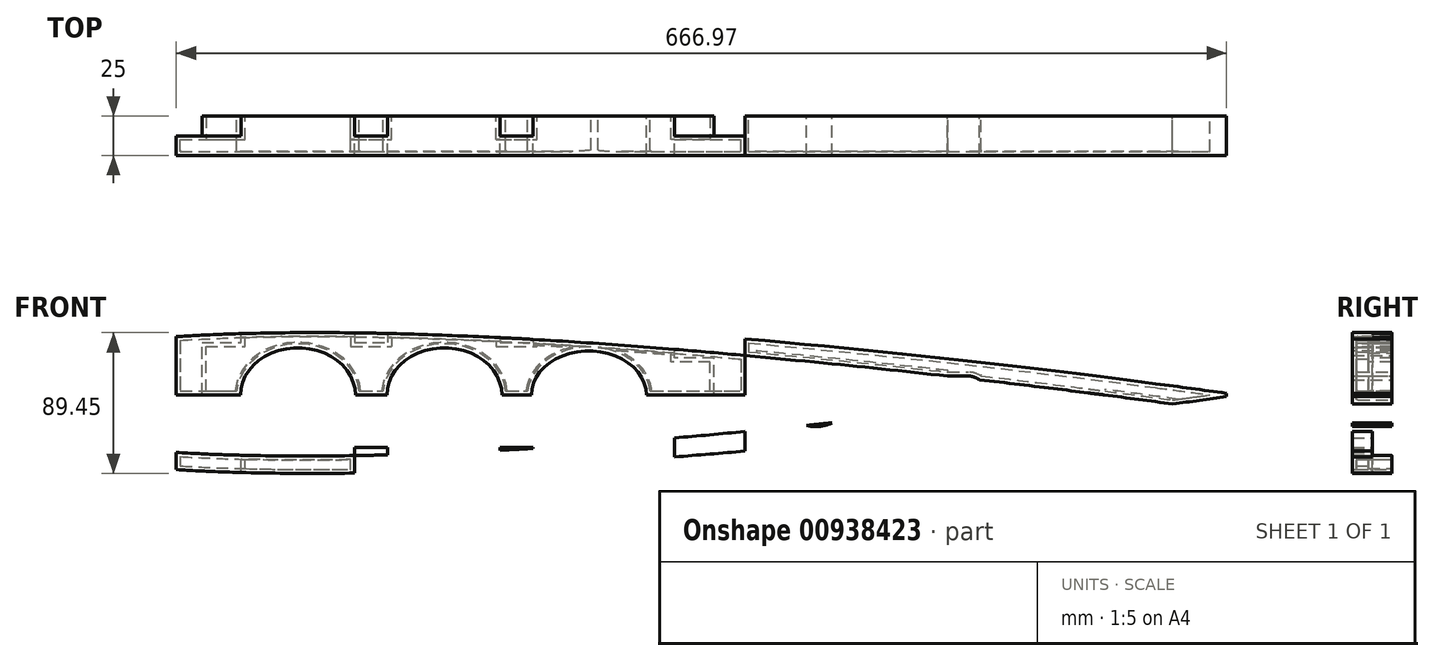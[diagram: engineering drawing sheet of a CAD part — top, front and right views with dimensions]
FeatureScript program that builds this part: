
annotation { "Feature Type Name" : "Feature", "Feature Type Description" : "" }
export const myFeature = defineFeature(function(context is Context, id is Id, definition is map)
    precondition{}
    {
        {
            var Q0;
            Q0=qCreatedBy(makeId("Front.planeOp"),FACE);
            var sketch = newSketch(context, id + "F0", { "sketchPlane" : qUnion([Q0])});
            skLineSegment(sketch, "E0", {"start": v(0, 0) * mm, "end": v(830, 0) * mm});
            skLineSegment(sketch, "E1", {"start": v(23.53, 0) * mm, "end": v(23.53, 22.98) * mm, "construction": true});
            skLineSegment(sketch, "E2", {"start": v(30.64, 0) * mm, "end": v(30.64, 25.86) * mm, "construction": true});
            skLineSegment(sketch, "E3", {"start": v(38.65, 0) * mm, "end": v(38.65, 28.62) * mm, "construction": true});
            skLineSegment(sketch, "E4", {"start": v(47.54, 0) * mm, "end": v(47.54, 31.24) * mm, "construction": true});
            skLineSegment(sketch, "E5", {"start": v(57.28, 0) * mm, "end": v(57.28, 33.72) * mm, "construction": true});
            skLineSegment(sketch, "E6", {"start": v(67.86, 0) * mm, "end": v(67.86, 36.05) * mm, "construction": true});
            skLineSegment(sketch, "E7", {"start": v(79.26, 0) * mm, "end": v(79.26, 38.22) * mm, "construction": true});
            skLineSegment(sketch, "E8", {"start": v(91.44, 0) * mm, "end": v(91.44, 40.22) * mm, "construction": true});
            skLineSegment(sketch, "E9", {"start": v(104.37, 0) * mm, "end": v(104.37, 42.04) * mm, "construction": true});
            skLineSegment(sketch, "E10", {"start": v(118.03, 0) * mm, "end": v(118.03, 43.68) * mm, "construction": true});
            skLineSegment(sketch, "E11", {"start": v(132.38, 0) * mm, "end": v(132.38, 45.13) * mm, "construction": true});
            skLineSegment(sketch, "E12", {"start": v(147.4, 0) * mm, "end": v(147.4, 46.38) * mm, "construction": true});
            skLineSegment(sketch, "E13", {"start": v(163.03, 0) * mm, "end": v(163.03, 47.45) * mm, "construction": true});
            skLineSegment(sketch, "E14", {"start": v(179.25, 0) * mm, "end": v(179.25, 48.31) * mm, "construction": true});
            skLineSegment(sketch, "E15", {"start": v(196.03, 0) * mm, "end": v(196.03, 48.98) * mm, "construction": true});
            skLineSegment(sketch, "E16", {"start": v(213.32, 0) * mm, "end": v(213.32, 49.45) * mm, "construction": true});
            skLineSegment(sketch, "E17", {"start": v(231.08, 0) * mm, "end": v(231.08, 49.73) * mm, "construction": true});
            skLineSegment(sketch, "E18", {"start": v(249.26, 0) * mm, "end": v(249.26, 49.81) * mm, "construction": true});
            skLineSegment(sketch, "E19", {"start": v(267.84, 0) * mm, "end": v(267.84, 49.72) * mm, "construction": true});
            skLineSegment(sketch, "E20", {"start": v(0.48, 0) * mm, "end": v(0.48, 3.54) * mm, "construction": true});
            skLineSegment(sketch, "E21", {"start": v(1.94, 0) * mm, "end": v(1.94, 7) * mm, "construction": true});
            skLineSegment(sketch, "E22", {"start": v(4.35, 0) * mm, "end": v(4.35, 10.38) * mm, "construction": true});
            skLineSegment(sketch, "E23", {"start": v(7.73, 0) * mm, "end": v(7.73, 13.67) * mm, "construction": true});
            skLineSegment(sketch, "E24", {"start": v(12.06, 0) * mm, "end": v(12.06, 16.87) * mm, "construction": true});
            skLineSegment(sketch, "E25", {"start": v(17.33, 0) * mm, "end": v(17.33, 19.98) * mm, "construction": true});
            skLineSegment(sketch, "E26", {"start": v(286.76, 0) * mm, "end": v(286.76, 49.45) * mm, "construction": true});
            skLineSegment(sketch, "E27", {"start": v(305.98, 0) * mm, "end": v(305.98, 49) * mm, "construction": true});
            skLineSegment(sketch, "E28", {"start": v(325.45, 0) * mm, "end": v(325.45, 48.4) * mm, "construction": true});
            skLineSegment(sketch, "E29", {"start": v(345.13, 0) * mm, "end": v(345.13, 47.64) * mm, "construction": true});
            skLineSegment(sketch, "E30", {"start": v(364.98, 0) * mm, "end": v(364.98, 46.75) * mm, "construction": true});
            skLineSegment(sketch, "E31", {"start": v(384.94, 0) * mm, "end": v(384.94, 45.71) * mm, "construction": true});
            skLineSegment(sketch, "E32", {"start": v(404.97, 0) * mm, "end": v(404.97, 44.56) * mm, "construction": true});
            skLineSegment(sketch, "E33", {"start": v(425.03, 0) * mm, "end": v(425.03, 43.3) * mm, "construction": true});
            skLineSegment(sketch, "E34", {"start": v(445.06, 0) * mm, "end": v(445.06, 41.93) * mm, "construction": true});
            skLineSegment(sketch, "E35", {"start": v(465.02, 0) * mm, "end": v(465.02, 40.47) * mm, "construction": true});
            skLineSegment(sketch, "E36", {"start": v(484.87, 0) * mm, "end": v(484.87, 38.94) * mm, "construction": true});
            skLineSegment(sketch, "E37", {"start": v(504.55, 0) * mm, "end": v(504.55, 37.33) * mm, "construction": true});
            skLineSegment(sketch, "E38", {"start": v(524.02, 0) * mm, "end": v(524.02, 35.67) * mm, "construction": true});
            skLineSegment(sketch, "E39", {"start": v(543.24, 0) * mm, "end": v(543.24, 33.96) * mm, "construction": true});
            skLineSegment(sketch, "E40", {"start": v(562.16, 0) * mm, "end": v(562.16, 32.21) * mm, "construction": true});
            skLineSegment(sketch, "E41", {"start": v(580.74, 0) * mm, "end": v(580.74, 30.44) * mm, "construction": true});
            skLineSegment(sketch, "E42", {"start": v(598.92, 0) * mm, "end": v(598.92, 28.64) * mm, "construction": true});
            skLineSegment(sketch, "E43", {"start": v(633.97, 0) * mm, "end": v(633.97, 25.03) * mm, "construction": true});
            skLineSegment(sketch, "E44", {"start": v(616.68, 0) * mm, "end": v(616.68, 26.83) * mm, "construction": true});
            skLineSegment(sketch, "E45", {"start": v(650.75, 0) * mm, "end": v(650.75, 23.23) * mm, "construction": true});
            skLineSegment(sketch, "E46", {"start": v(666.97, 0) * mm, "end": v(666.97, 21.44) * mm, "construction": true});
            skLineSegment(sketch, "E47", {"start": v(682.6, 0) * mm, "end": v(682.6, 19.68) * mm, "construction": true});
            skLineSegment(sketch, "E48", {"start": v(697.62, 0) * mm, "end": v(697.62, 17.96) * mm, "construction": true});
            skLineSegment(sketch, "E49", {"start": v(711.97, 0) * mm, "end": v(711.97, 16.27) * mm, "construction": true});
            skLineSegment(sketch, "E50", {"start": v(725.63, 0) * mm, "end": v(725.63, 14.64) * mm, "construction": true});
            skLineSegment(sketch, "E51", {"start": v(738.56, 0) * mm, "end": v(738.56, 13.06) * mm, "construction": true});
            skLineSegment(sketch, "E52", {"start": v(750.74, 0) * mm, "end": v(750.74, 11.55) * mm, "construction": true});
            skLineSegment(sketch, "E53", {"start": v(762.14, 0) * mm, "end": v(762.14, 10.11) * mm, "construction": true});
            skLineSegment(sketch, "E54", {"start": v(791.35, 0) * mm, "end": v(791.35, 6.32) * mm, "construction": true});
            skLineSegment(sketch, "E55", {"start": v(799.36, 0) * mm, "end": v(799.36, 5.25) * mm, "construction": true});
            skLineSegment(sketch, "E56", {"start": v(806.47, 0) * mm, "end": v(806.47, 4.29) * mm, "construction": true});
            skLineSegment(sketch, "E57", {"start": v(782.46, 0) * mm, "end": v(782.46, 7.49) * mm, "construction": true});
            skLineSegment(sketch, "E58", {"start": v(812.67, 0) * mm, "end": v(812.67, 3.45) * mm, "construction": true});
            skLineSegment(sketch, "E59", {"start": v(817.94, 0) * mm, "end": v(817.94, 2.72) * mm, "construction": true});
            skLineSegment(sketch, "E60", {"start": v(822.27, 0) * mm, "end": v(822.27, 2.12) * mm, "construction": true});
            skLineSegment(sketch, "E61", {"start": v(825.65, 0) * mm, "end": v(825.65, 1.65) * mm, "construction": true});
            skLineSegment(sketch, "E62", {"start": v(828.06, 0) * mm, "end": v(828.06, 1.32) * mm, "construction": true});
            skLineSegment(sketch, "E63", {"start": v(772.72, 0) * mm, "end": v(772.72, 8.76) * mm, "construction": true});
            skLineSegment(sketch, "E64", {"start": v(829.52, 0) * mm, "end": v(829.52, 1.11) * mm, "construction": true});
            skLineSegment(sketch, "E65", {"start": v(830, 0) * mm, "end": v(830, 1.05) * mm});
            skFitSpline(sketch, "E66", {"points": [v(0, 0) * mm, v(0.48, 3.54) * mm, v(1.94, 7) * mm, v(4.35, 10.38) * mm, v(7.73, 13.67) * mm, v(12.06, 16.87) * mm, v(17.33, 19.98) * mm, v(23.53, 22.98) * mm, v(30.64, 25.86) * mm, v(38.65, 28.62) * mm, v(47.54, 31.24) * mm, v(57.28, 33.72) * mm, v(67.86, 36.05) * mm, v(79.26, 38.22) * mm, v(91.44, 40.22) * mm, v(104.37, 42.04) * mm, v(118.03, 43.68) * mm, v(132.38, 45.13) * mm, v(147.4, 46.39) * mm, v(163.03, 47.45) * mm, v(179.25, 48.31) * mm, v(196.03, 48.98) * mm, v(213.32, 49.45) * mm, v(231.08, 49.73) * mm, v(249.26, 49.81) * mm, v(267.84, 49.72) * mm, v(286.76, 49.45) * mm, v(305.98, 49) * mm, v(325.45, 48.4) * mm, v(345.13, 47.64) * mm, v(364.98, 46.75) * mm, v(384.94, 45.71) * mm, v(404.97, 44.56) * mm, v(425.03, 43.3) * mm, v(445.06, 41.93) * mm, v(465.02, 40.47) * mm, v(484.87, 38.94) * mm, v(504.55, 37.33) * mm, v(524.02, 35.67) * mm, v(543.24, 33.96) * mm, v(562.16, 32.21) * mm, v(580.74, 30.44) * mm, v(598.92, 28.64) * mm, v(616.68, 26.83) * mm, v(633.97, 25.03) * mm, v(650.75, 23.23) * mm, v(666.97, 21.44) * mm, v(682.6, 19.68) * mm, v(697.62, 17.96) * mm, v(711.97, 16.27) * mm, v(725.63, 14.64) * mm, v(738.56, 13.06) * mm, v(750.74, 11.55) * mm, v(762.14, 10.11) * mm, v(772.72, 8.76) * mm, v(782.46, 7.49) * mm, v(791.35, 6.32) * mm, v(799.36, 5.25) * mm, v(806.47, 4.29) * mm, v(812.67, 3.45) * mm, v(817.94, 2.72) * mm, v(822.27, 2.12) * mm, v(825.65, 1.65) * mm, v(828.06, 1.32) * mm, v(829.52, 1.11) * mm, v(830, 1.05) * mm], "startDerivative": vector(34.1, 427.03) * mm, "endDerivative": vector(137.1, -19.25) * mm});
            skFitSpline(sketch, "E67.MirrorCS", {"points": [v(0, 0) * mm, v(0.48, -3.54) * mm, v(1.94, -7) * mm, v(4.35, -10.38) * mm, v(7.73, -13.67) * mm, v(12.06, -16.87) * mm, v(17.33, -19.98) * mm, v(23.53, -22.98) * mm, v(30.64, -25.86) * mm, v(38.65, -28.62) * mm, v(47.54, -31.24) * mm, v(57.28, -33.72) * mm, v(67.86, -36.05) * mm, v(79.26, -38.22) * mm, v(91.44, -40.22) * mm, v(104.37, -42.04) * mm, v(118.03, -43.68) * mm, v(132.38, -45.13) * mm, v(147.4, -46.39) * mm, v(163.03, -47.45) * mm, v(179.25, -48.31) * mm, v(196.03, -48.98) * mm, v(213.32, -49.45) * mm, v(231.08, -49.73) * mm, v(249.26, -49.81) * mm, v(267.84, -49.72) * mm, v(286.76, -49.45) * mm, v(305.98, -49) * mm, v(325.45, -48.4) * mm, v(345.13, -47.64) * mm, v(364.98, -46.75) * mm, v(384.94, -45.71) * mm, v(404.97, -44.56) * mm, v(425.03, -43.3) * mm, v(445.06, -41.93) * mm, v(465.02, -40.47) * mm, v(484.87, -38.94) * mm, v(504.55, -37.33) * mm, v(524.02, -35.67) * mm, v(543.24, -33.96) * mm, v(562.16, -32.21) * mm, v(580.74, -30.44) * mm, v(598.92, -28.64) * mm, v(616.68, -26.83) * mm, v(633.97, -25.03) * mm, v(650.75, -23.23) * mm, v(666.97, -21.44) * mm, v(682.6, -19.68) * mm, v(697.62, -17.96) * mm, v(711.97, -16.27) * mm, v(725.63, -14.64) * mm, v(738.56, -13.06) * mm, v(750.74, -11.55) * mm, v(762.14, -10.11) * mm, v(772.72, -8.76) * mm, v(782.46, -7.49) * mm, v(791.35, -6.32) * mm, v(799.36, -5.25) * mm, v(806.47, -4.29) * mm, v(812.67, -3.45) * mm, v(817.94, -2.72) * mm, v(822.27, -2.12) * mm, v(825.65, -1.65) * mm, v(828.06, -1.32) * mm, v(829.52, -1.11) * mm, v(830, -1.05) * mm], "startDerivative": vector(34.1, -427.03) * mm, "endDerivative": vector(137.1, 19.25) * mm});
            skLineSegment(sketch, "E68.MirrorCS", {"start": v(830, 0) * mm, "end": v(830, -1.05) * mm});
            skLineSegment(sketch, "E69", {"start": v(163.03, 47.45) * mm, "end": v(163.03, -47.45) * mm});
            skLineSegment(sketch, "E70", {"start": v(204.25, -49.23) * mm, "end": v(204.25, -33.23) * mm});
            skLineSegment(sketch, "E71", {"start": v(204.25, -33.23) * mm, "end": v(179.25, -33.23) * mm});
            skLineSegment(sketch, "E72", {"start": v(179.25, -33.23) * mm, "end": v(179.25, 33.23) * mm});
            skLineSegment(sketch, "E73", {"start": v(179.25, 33.23) * mm, "end": v(204.25, 33.23) * mm});
            skLineSegment(sketch, "E74", {"start": v(204.25, 33.23) * mm, "end": v(204.25, 49.23) * mm});
            skLineSegment(sketch, "E75", {"start": v(524.02, 35.67) * mm, "end": v(524.02, -35.67) * mm});
            skLineSegment(sketch, "E76", {"start": v(479.55, -39.36) * mm, "end": v(479.55, -23.36) * mm});
            skLineSegment(sketch, "E77", {"start": v(479.55, -23.36) * mm, "end": v(504.55, -23.36) * mm});
            skLineSegment(sketch, "E78", {"start": v(504.55, -23.36) * mm, "end": v(504.55, 23.36) * mm});
            skLineSegment(sketch, "E79", {"start": v(504.55, 23.36) * mm, "end": v(479.55, 23.36) * mm});
            skLineSegment(sketch, "E80", {"start": v(479.55, 23.36) * mm, "end": v(479.55, 39.36) * mm});
            skEllipse(sketch, "E81", {"center": v(240.25, 0) * mm, "majorRadius": 36.5 * mm, "minorRadius": 30 * mm, "majorAxis": v(1, 0)});
            skEllipse(sketch, "E82.1.0.0", {"center": v(333.25, 0) * mm, "majorRadius": 36.5 * mm, "minorRadius": 30 * mm, "majorAxis": v(1, 0)});
            skLineSegment(sketch, "E82.direction1", {"start": v(240.25, 0) * mm, "end": v(333.25, 0) * mm, "construction": true});
            skEllipse(sketch, "E83", {"center": v(425.03, 0) * mm, "majorRadius": 28 * mm, "minorRadius": 36.5 * mm, "majorAxis": v(0, -1)});
            skFitSpline(sketch, "E84.0", {"points": [v(19.9, 0) * mm, v(19.93, 0.28) * mm, v(19.97, 0.77) * mm, v(20.03, 1.33) * mm, v(20.07, 1.63) * mm, v(20.1, 1.78) * mm, v(20.12, 1.85) * mm, v(20.12, 1.88) * mm, v(20.13, 1.92) * mm, v(20.16, 1.99) * mm, v(20.2, 2.1) * mm, v(20.28, 2.3) * mm, v(20.43, 2.58) * mm, v(20.63, 2.94) * mm, v(20.87, 3.32) * mm, v(21.13, 3.7) * mm, v(21.53, 4.23) * mm, v(22.12, 4.91) * mm, v(22.98, 5.8) * mm, v(24.01, 6.71) * mm, v(25.19, 7.65) * mm, v(26.5, 8.6) * mm, v(28.4, 9.86) * mm, v(31.06, 11.42) * mm, v(34.64, 13.25) * mm, v(38.55, 15) * mm, v(44.15, 17.24) * mm, v(51.77, 19.86) * mm, v(61.74, 22.7) * mm, v(72.4, 25.26) * mm, v(83.62, 27.56) * mm, v(95.37, 29.62) * mm, v(107.56, 31.45) * mm, v(124.36, 33.6) * mm, v(146.26, 35.8) * mm, v(173.73, 37.69) * mm, v(202.17, 38.91) * mm, v(231.43, 39.53) * mm, v(261.35, 39.6) * mm, v(291.8, 39.18) * mm, v(322.69, 38.31) * mm, v(364.28, 36.62) * mm, v(416.8, 33.63) * mm, v(479.93, 28.95) * mm, v(531.98, 24.38) * mm, v(572.9, 20.44) * mm, v(603.14, 17.37) * mm, v(632.79, 14.2) * mm, v(661.73, 10.99) * mm, v(689.84, 7.73) * mm, v(716.93, 4.47) * mm, v(738.52, 1.78) * mm, v(755.07, -0.33) * mm, v(767.08, -1.9) * mm, v(778.65, -3.43) * mm, v(789.72, -4.91) * mm, v(800.24, -6.35) * mm, v(810.11, -7.7) * mm, v(817.7, -8.77) * mm, v(823.32, -9.57) * mm, v(826.6, -10.03) * mm, v(829.07, -10.39) * mm, v(830.84, -10.64) * mm, v(832.51, -10.88) * mm, v(834.08, -11.1) * mm, v(835.26, -11.27) * mm, v(836.14, -11.4) * mm, v(836.78, -11.5) * mm, v(837.37, -11.58) * mm, v(837.78, -11.64) * mm, v(838.05, -11.68) * mm, v(838.28, -11.71) * mm, v(838.4, -11.73) * mm, v(838.5, -11.74) * mm]});
            skFitSpline(sketch, "E85.MirrorCS", {"points": [v(19.9, 0) * mm, v(19.93, -0.28) * mm, v(19.97, -0.77) * mm, v(20.03, -1.33) * mm, v(20.08, -1.63) * mm, v(20.1, -1.78) * mm, v(20.12, -1.85) * mm, v(20.13, -1.87) * mm, v(20.14, -1.92) * mm, v(20.16, -1.99) * mm, v(20.2, -2.1) * mm, v(20.29, -2.29) * mm, v(20.44, -2.58) * mm, v(20.64, -2.94) * mm, v(20.88, -3.31) * mm, v(21.15, -3.7) * mm, v(21.55, -4.22) * mm, v(22.13, -4.9) * mm, v(23, -5.78) * mm, v(24.04, -6.7) * mm, v(25.22, -7.63) * mm, v(26.52, -8.57) * mm, v(28.44, -9.83) * mm, v(31.1, -11.38) * mm, v(34.7, -13.2) * mm, v(38.6, -14.93) * mm, v(44.21, -17.15) * mm, v(51.85, -19.74) * mm, v(61.83, -22.54) * mm, v(72.49, -25.06) * mm, v(83.73, -27.32) * mm, v(95.48, -29.34) * mm, v(107.68, -31.12) * mm, v(124.49, -33.22) * mm, v(146.4, -35.32) * mm, v(173.87, -37.11) * mm, v(202.32, -38.23) * mm, v(231.57, -38.74) * mm, v(261.5, -38.7) * mm, v(291.95, -38.16) * mm, v(322.83, -37.18) * mm, v(364.42, -35.33) * mm, v(416.93, -32.14) * mm, v(480.03, -27.22) * mm, v(532.07, -22.46) * mm, v(572.98, -18.36) * mm, v(603.2, -15.18) * mm, v(632.84, -11.91) * mm, v(661.77, -8.58) * mm, v(689.86, -5.22) * mm, v(716.95, -1.86) * mm, v(738.52, 0.91) * mm, v(755.06, 3.1) * mm, v(767.06, 4.7) * mm, v(778.63, 6.27) * mm, v(789.7, 7.8) * mm, v(800.21, 9.27) * mm, v(810.08, 10.67) * mm, v(817.67, 11.77) * mm, v(823.28, 12.58) * mm, v(826.56, 13.06) * mm, v(829.03, 13.42) * mm, v(830.8, 13.68) * mm, v(832.47, 13.93) * mm, v(834.03, 14.16) * mm, v(835.21, 14.33) * mm, v(836.1, 14.46) * mm, v(836.73, 14.56) * mm, v(837.32, 14.64) * mm, v(837.73, 14.7) * mm, v(838, 14.75) * mm, v(838.23, 14.78) * mm, v(838.36, 14.8) * mm, v(838.45, 14.81) * mm]});
            skLineSegment(sketch, "E86", {"start": v(100.03, 30.3) * mm, "end": v(134.03, 30.3) * mm});
            skLineSegment(sketch, "E87", {"start": v(140.03, 24.3) * mm, "end": v(140.03, -24.26) * mm});
            skLineSegment(sketch, "E88", {"start": v(133.98, -30.26) * mm, "end": v(100.03, -29.99) * mm});
            skPoint(sketch, "E89.visualSharp", {"position": v(140.03, 30.3) * mm});
            skArc(sketch, "E89.filletArc", {"start": v(140.03, 24.3) * mm, "mid": v(138.27, 28.55) * mm, "end": v(134.03, 30.3) * mm});
            skPoint(sketch, "E90.visualSharp", {"position": v(140.03, -30.3) * mm});
            skArc(sketch, "E90.filletArc", {"start": v(133.98, -30.26) * mm, "mid": v(138.25, -28.52) * mm, "end": v(140.03, -24.26) * mm});
            skEllipse(sketch, "E91", {"center": v(569.02, 0) * mm, "majorRadius": 20 * mm, "minorRadius": 22.5 * mm, "majorAxis": v(0, -1)});
            skLineSegment(sketch, "E92.bottom", {"start": v(625.97, -12) * mm, "end": v(665.97, -12) * mm});
            skLineSegment(sketch, "E92.top", {"start": v(625.97, 12) * mm, "end": v(665.97, 12) * mm});
            skLineSegment(sketch, "E92.left", {"start": v(623.97, -10) * mm, "end": v(623.97, 10) * mm});
            skLineSegment(sketch, "E92.right", {"start": v(665.97, -12) * mm, "end": v(665.97, 12) * mm});
            skPoint(sketch, "E92.middle", {"position": v(644.97, 0) * mm});
            skArc(sketch, "E93", {"start": v(665.97, 12) * mm, "mid": v(677.97, 0) * mm, "end": v(665.97, -12) * mm});
            skPoint(sketch, "E94.visualSharp", {"position": v(623.97, 12) * mm});
            skArc(sketch, "E94.filletArc", {"start": v(625.97, 12) * mm, "mid": v(624.56, 11.41) * mm, "end": v(623.97, 10) * mm});
            skPoint(sketch, "E95.visualSharp", {"position": v(623.97, -12) * mm});
            skArc(sketch, "E95.filletArc", {"start": v(623.97, -10) * mm, "mid": v(624.56, -11.41) * mm, "end": v(625.97, -12) * mm});
            skPoint(sketch, "E96", {"position": v(276.75, 0) * mm});
            skPoint(sketch, "E97", {"position": v(296.75, 0) * mm});
            skLineSegment(sketch, "E98.bottom", {"start": v(276.26, 65.67) * mm, "end": v(297.26, 65.67) * mm});
            skLineSegment(sketch, "E98.top", {"start": v(276.26, 33.23) * mm, "end": v(297.26, 33.23) * mm});
            skLineSegment(sketch, "E98.left", {"start": v(276.26, 65.67) * mm, "end": v(276.26, 33.23) * mm});
            skLineSegment(sketch, "E98.right", {"start": v(297.26, 65.67) * mm, "end": v(297.26, 33.23) * mm});
            skPoint(sketch, "E99", {"position": v(369.75, 0) * mm});
            skPoint(sketch, "E100", {"position": v(388.53, 0) * mm});
            skLineSegment(sketch, "E101", {"start": v(379.14, 0) * mm, "end": v(379.14, 46.03) * mm, "construction": true});
            skLineSegment(sketch, "E102.bottom", {"start": v(368.64, 58.81) * mm, "end": v(389.64, 58.81) * mm});
            skLineSegment(sketch, "E102.top", {"start": v(368.64, 33.23) * mm, "end": v(389.64, 33.23) * mm});
            skLineSegment(sketch, "E102.left", {"start": v(368.64, 58.81) * mm, "end": v(368.64, 33.23) * mm});
            skLineSegment(sketch, "E102.right", {"start": v(389.64, 58.81) * mm, "end": v(389.64, 33.23) * mm});
            skLineSegment(sketch, "E103.MirrorCS", {"start": v(297.26, -65.67) * mm, "end": v(297.26, -33.23) * mm});
            skLineSegment(sketch, "E104.MirrorCS", {"start": v(276.26, -65.67) * mm, "end": v(297.26, -65.67) * mm});
            skLineSegment(sketch, "E105.MirrorCS", {"start": v(276.26, -65.67) * mm, "end": v(276.26, -33.23) * mm});
            skLineSegment(sketch, "E106.MirrorCS", {"start": v(276.26, -33.23) * mm, "end": v(297.26, -33.23) * mm});
            skLineSegment(sketch, "E107.MirrorCS", {"start": v(368.64, -58.81) * mm, "end": v(389.64, -58.81) * mm});
            skLineSegment(sketch, "E108.MirrorCS", {"start": v(368.64, -58.81) * mm, "end": v(368.64, -33.23) * mm});
            skLineSegment(sketch, "E109.MirrorCS", {"start": v(389.64, -58.81) * mm, "end": v(389.64, -33.23) * mm});
            skLineSegment(sketch, "E110.MirrorCS", {"start": v(368.64, -33.23) * mm, "end": v(389.64, -33.23) * mm});
            skSolve(sketch);
        }
        {
            var Q0;
            {var subQ5=sQuery(id+"F0.wireOp",EDGE,"E84.0");Q0=makeQuery(id+"F0.imprint","IMPRINT",FACE,{"disambiguationData":[TD([[makeQuery(id+"F0.imprint","IMPRINT",EDGE,{"derivedFrom":subQ5}),1.0]])]});}
            var Q1;
            {var subQ6=sQuery(id+"F0.wireOp",EDGE,"E85.MirrorCS");Q1=makeQuery(id+"F0.imprint","IMPRINT",FACE,{"disambiguationData":[TD([[makeQuery(id+"F0.imprint","IMPRINT",EDGE,{"derivedFrom":subQ6}),-1.0]])]});}
            var Q2;
            {var subQ4=sQuery(id+"F0.wireOp",EDGE,"E73");Q2=makeQuery(id+"F0.imprint","IMPRINT",FACE,{"disambiguationData":[TD([[makeQuery(id+"F0.imprint","IMPRINT",EDGE,{"derivedFrom":subQ4}),1.0]])]});}
            var Q3;
            {var subQ0=sQuery(id+"F0.wireOp",EDGE,"E70");Q3=makeQuery(id+"F0.imprint","IMPRINT",FACE,{"disambiguationData":[TD([[makeQuery(id+"F0.imprint","IMPRINT",EDGE,{"derivedFrom":subQ0}),1.0]])]});}
            var Q4;
            {var subQ4=sQuery(id+"F0.wireOp",EDGE,"E70");Q4=makeQuery(id+"F0.imprint","IMPRINT",FACE,{"disambiguationData":[TD([[makeQuery(id+"F0.imprint","IMPRINT",EDGE,{"derivedFrom":subQ4}),-1.0]])]});}
            var Q5;
            {var subQ0=sQuery(id+"F0.wireOp",EDGE,"E73");Q5=makeQuery(id+"F0.imprint","IMPRINT",FACE,{"disambiguationData":[TD([[makeQuery(id+"F0.imprint","IMPRINT",EDGE,{"derivedFrom":subQ0}),-1.0]])]});}
            var Q6;
            {var subQ0=sQuery(id+"F0.wireOp",EDGE,"E79");Q6=makeQuery(id+"F0.imprint","IMPRINT",FACE,{"disambiguationData":[TD([[makeQuery(id+"F0.imprint","IMPRINT",EDGE,{"derivedFrom":subQ0}),-1.0]])]});}
            var Q7;
            {var subQ0=sQuery(id+"F0.wireOp",EDGE,"E76");Q7=makeQuery(id+"F0.imprint","IMPRINT",FACE,{"disambiguationData":[TD([[makeQuery(id+"F0.imprint","IMPRINT",EDGE,{"derivedFrom":subQ0}),-1.0]])]});}
            var Q8;
            {var subQ8=sQuery(id+"F0.wireOp",EDGE,"E68.MirrorCS");Q8=makeQuery(id+"F0.imprint","IMPRINT",FACE,{"disambiguationData":[TD([[makeQuery(id+"F0.imprint","IMPRINT",EDGE,{"derivedFrom":subQ8}),-1.0]])]});}
            var Q9;
            {var subQ11=sQuery(id+"F0.wireOp",EDGE,"E65");Q9=makeQuery(id+"F0.imprint","IMPRINT",FACE,{"disambiguationData":[TD([[makeQuery(id+"F0.imprint","IMPRINT",EDGE,{"derivedFrom":subQ11}),1.0]])]});}
            var Q10;
            {var subQ5=sQuery(id+"F0.wireOp",EDGE,"E98.top");Q10=makeQuery(id+"F0.imprint","IMPRINT",FACE,{"disambiguationData":[TD([[makeQuery(id+"F0.imprint","IMPRINT",EDGE,{"derivedFrom":subQ5}),1.0]])]});}
            var Q11;
            {var subQ5=sQuery(id+"F0.wireOp",EDGE,"E102.top");Q11=makeQuery(id+"F0.imprint","IMPRINT",FACE,{"disambiguationData":[TD([[makeQuery(id+"F0.imprint","IMPRINT",EDGE,{"derivedFrom":subQ5}),1.0]])]});}
            var Q12;
            {var subQ5=sQuery(id+"F0.wireOp",EDGE,"E110.MirrorCS");Q12=makeQuery(id+"F0.imprint","IMPRINT",FACE,{"disambiguationData":[TD([[makeQuery(id+"F0.imprint","IMPRINT",EDGE,{"derivedFrom":subQ5}),-1.0]])]});}
            var Q13;
            {var subQ5=sQuery(id+"F0.wireOp",EDGE,"E106.MirrorCS");Q13=makeQuery(id+"F0.imprint","IMPRINT",FACE,{"disambiguationData":[TD([[makeQuery(id+"F0.imprint","IMPRINT",EDGE,{"derivedFrom":subQ5}),-1.0]])]});}
            extrude(context, id + "F1", {"entities" : qUnion([Q0, Q1, Q2, Q3, Q4, Q5, Q6, Q7, Q8, Q9, Q10, Q11, Q12, Q13]), "depth" : 12.5 * mm, "offsetDistance" : 25 * mm});
        }
        {
            var Q0;
            {var subQ0=sQuery(id+"F0.wireOp",EDGE,"E73");Q0=makeQuery(id+"F0.imprint","IMPRINT",FACE,{"disambiguationData":[TD([[makeQuery(id+"F0.imprint","IMPRINT",EDGE,{"derivedFrom":subQ0}),-1.0]])]});}
            var Q1;
            {var subQ4=sQuery(id+"F0.wireOp",EDGE,"E70");Q1=makeQuery(id+"F0.imprint","IMPRINT",FACE,{"disambiguationData":[TD([[makeQuery(id+"F0.imprint","IMPRINT",EDGE,{"derivedFrom":subQ4}),-1.0]])]});}
            var Q2;
            {var subQ11=sQuery(id+"F0.wireOp",EDGE,"E65");Q2=makeQuery(id+"F0.imprint","IMPRINT",FACE,{"disambiguationData":[TD([[makeQuery(id+"F0.imprint","IMPRINT",EDGE,{"derivedFrom":subQ11}),1.0]])]});}
            var Q3;
            {var subQ8=sQuery(id+"F0.wireOp",EDGE,"E68.MirrorCS");Q3=makeQuery(id+"F0.imprint","IMPRINT",FACE,{"disambiguationData":[TD([[makeQuery(id+"F0.imprint","IMPRINT",EDGE,{"derivedFrom":subQ8}),-1.0]])]});}
            var Q4;
            {var subQ5=sQuery(id+"F0.wireOp",EDGE,"E84.0");Q4=makeQuery(id+"F0.imprint","IMPRINT",FACE,{"disambiguationData":[TD([[makeQuery(id+"F0.imprint","IMPRINT",EDGE,{"derivedFrom":subQ5}),1.0]])]});}
            var Q5;
            {var subQ6=sQuery(id+"F0.wireOp",EDGE,"E85.MirrorCS");Q5=makeQuery(id+"F0.imprint","IMPRINT",FACE,{"disambiguationData":[TD([[makeQuery(id+"F0.imprint","IMPRINT",EDGE,{"derivedFrom":subQ6}),-1.0]])]});}
            extrude(context, id + "F2", {"entities" : qUnion([Q0, Q1, Q2, Q3, Q4, Q5]), "operationType" : NewBodyOperationType.ADD, "oppositeDirection" : true, "depth" : 12.5 * mm, "offsetDistance" : 25 * mm});
        }
        {
            var Q0;
            Q0=makeQuery(id+"F2.opExtrude","CAP_FACE",FACE,{"disambiguationData":[OSD([sQuery(id+"F0.wireOp",EDGE,"E66"),sQuery(id+"F0.wireOp",EDGE,"E67.MirrorCS"),sQuery(id+"F0.wireOp",EDGE,"E70"),sQuery(id+"F0.wireOp",EDGE,"E71"),sQuery(id+"F0.wireOp",EDGE,"E72"),sQuery(id+"F0.wireOp",EDGE,"E73"),sQuery(id+"F0.wireOp",EDGE,"E74"),sQuery(id+"F0.wireOp",EDGE,"E76"),sQuery(id+"F0.wireOp",EDGE,"E77"),sQuery(id+"F0.wireOp",EDGE,"E78"),sQuery(id+"F0.wireOp",EDGE,"E79"),sQuery(id+"F0.wireOp",EDGE,"E80"),sQuery(id+"F0.wireOp",EDGE,"E81"),sQuery(id+"F0.wireOp",EDGE,"E82.1.0.0"),sQuery(id+"F0.wireOp",EDGE,"E83"),sQuery(id+"F0.wireOp",EDGE,"E98.top"),sQuery(id+"F0.wireOp",EDGE,"E98.left"),sQuery(id+"F0.wireOp",EDGE,"E98.right"),sQuery(id+"F0.wireOp",EDGE,"E102.top"),sQuery(id+"F0.wireOp",EDGE,"E102.left"),sQuery(id+"F0.wireOp",EDGE,"E102.right"),sQuery(id+"F0.wireOp",EDGE,"E103.MirrorCS"),sQuery(id+"F0.wireOp",EDGE,"E105.MirrorCS"),sQuery(id+"F0.wireOp",EDGE,"E106.MirrorCS"),sQuery(id+"F0.wireOp",EDGE,"E108.MirrorCS"),sQuery(id+"F0.wireOp",EDGE,"E109.MirrorCS"),sQuery(id+"F0.wireOp",EDGE,"E110.MirrorCS")])],"isStart":false});
            var Q1;
            Q1=makeQuery(id+"F2.opExtrude","CAP_FACE",FACE,{"disambiguationData":[OSD([sQuery(id+"F0.wireOp",EDGE,"E65"),sQuery(id+"F0.wireOp",EDGE,"E66"),sQuery(id+"F0.wireOp",EDGE,"E67.MirrorCS"),sQuery(id+"F0.wireOp",EDGE,"E68.MirrorCS"),sQuery(id+"F0.wireOp",EDGE,"E75"),sQuery(id+"F0.wireOp",EDGE,"E91"),sQuery(id+"F0.wireOp",EDGE,"E92.bottom"),sQuery(id+"F0.wireOp",EDGE,"E92.top"),sQuery(id+"F0.wireOp",EDGE,"E92.left"),sQuery(id+"F0.wireOp",EDGE,"E93"),sQuery(id+"F0.wireOp",EDGE,"E94.filletArc"),sQuery(id+"F0.wireOp",EDGE,"E95.filletArc")])],"isStart":false});
            var Q2;
            Q2=makeQuery(id+"F2.opExtrude","CAP_FACE",FACE,{"disambiguationData":[OSD([sQuery(id+"F0.wireOp",EDGE,"E66"),sQuery(id+"F0.wireOp",EDGE,"E67.MirrorCS"),sQuery(id+"F0.wireOp",EDGE,"E69"),sQuery(id+"F0.wireOp",EDGE,"E84.0"),sQuery(id+"F0.wireOp",EDGE,"E85.MirrorCS"),sQuery(id+"F0.wireOp",EDGE,"E86"),sQuery(id+"F0.wireOp",EDGE,"E87"),sQuery(id+"F0.wireOp",EDGE,"E88"),sQuery(id+"F0.wireOp",EDGE,"E89.filletArc"),sQuery(id+"F0.wireOp",EDGE,"E90.filletArc")])],"isStart":false});
            shell(context, id + "F3", {"entities" : qUnion([Q0, Q1, Q2]), "thickness" : 2.5 * mm});
        }
        {
            var Q0;
            {var subQ0=sQuery(id+"F0.wireOp",EDGE,"E83");Q0=makeQuery(id+"F3.opShell","OFFSET_EDGE",EDGE,{"disambiguationData":[OSD([subQ0]),TDD([makeQuery(id+"F1.opExtrude","CAP_EDGE",EDGE,{"disambiguationData":[OSD([subQ0])],"isStart":false})])]});}
            var Q1;
            {var subQ0=sQuery(id+"F0.wireOp",EDGE,"E82.1.0.0");Q1=makeQuery(id+"F3.opShell","OFFSET_EDGE",EDGE,{"disambiguationData":[OSD([subQ0]),TDD([makeQuery(id+"F1.opExtrude","CAP_EDGE",EDGE,{"disambiguationData":[OSD([subQ0])],"isStart":false})])]});}
            var Q2;
            {var subQ0=sQuery(id+"F0.wireOp",EDGE,"E81");Q2=makeQuery(id+"F3.opShell","OFFSET_EDGE",EDGE,{"disambiguationData":[OSD([subQ0]),TDD([makeQuery(id+"F1.opExtrude","CAP_EDGE",EDGE,{"disambiguationData":[OSD([subQ0])],"isStart":false})])]});}
            var Q3;
            {var subQ0=sQuery(id+"F0.wireOp",EDGE,"E88");Q3=makeQuery(id+"F3.opShell","OFFSET_EDGE",EDGE,{"disambiguationData":[OSD([subQ0]),TDD([makeQuery(id+"F1.opExtrude","CAP_EDGE",EDGE,{"disambiguationData":[OSD([subQ0])],"isStart":false})])]});}
            var Q4;
            {var subQ0=sQuery(id+"F0.wireOp",EDGE,"E90.filletArc");Q4=makeQuery(id+"F3.opShell","OFFSET_EDGE",EDGE,{"disambiguationData":[OSD([subQ0]),TDD([makeQuery(id+"F1.opExtrude","CAP_EDGE",EDGE,{"disambiguationData":[OSD([subQ0])],"isStart":false})])]});}
            var Q5;
            {var subQ0=sQuery(id+"F0.wireOp",EDGE,"E87");Q5=makeQuery(id+"F3.opShell","OFFSET_EDGE",EDGE,{"disambiguationData":[OSD([subQ0]),TDD([makeQuery(id+"F1.opExtrude","CAP_EDGE",EDGE,{"disambiguationData":[OSD([subQ0])],"isStart":false})])]});}
            var Q6;
            {var subQ0=sQuery(id+"F0.wireOp",EDGE,"E85.MirrorCS");Q6=makeQuery(id+"F3.opShell","OFFSET_EDGE",EDGE,{"disambiguationData":[OSD([subQ0]),TDD([makeQuery(id+"F1.opExtrude","CAP_EDGE",EDGE,{"disambiguationData":[OSD([subQ0])],"isStart":false})])]});}
            var Q7;
            {var subQ0=sQuery(id+"F0.wireOp",EDGE,"E86");Q7=makeQuery(id+"F3.opShell","OFFSET_EDGE",EDGE,{"disambiguationData":[OSD([subQ0]),TDD([makeQuery(id+"F1.opExtrude","CAP_EDGE",EDGE,{"disambiguationData":[OSD([subQ0])],"isStart":false})])]});}
            var Q8;
            {var subQ0=sQuery(id+"F0.wireOp",EDGE,"E89.filletArc");Q8=makeQuery(id+"F3.opShell","OFFSET_EDGE",EDGE,{"disambiguationData":[OSD([subQ0]),TDD([makeQuery(id+"F1.opExtrude","CAP_EDGE",EDGE,{"disambiguationData":[OSD([subQ0])],"isStart":false})])]});}
            var Q9;
            {var subQ0=sQuery(id+"F0.wireOp",EDGE,"E84.0");Q9=makeQuery(id+"F3.opShell","OFFSET_EDGE",EDGE,{"disambiguationData":[OSD([subQ0]),TDD([makeQuery(id+"F1.opExtrude","CAP_EDGE",EDGE,{"disambiguationData":[OSD([subQ0])],"isStart":false})])]});}
            var Q10;
            {var subQ0=sQuery(id+"F0.wireOp",EDGE,"E92.top");Q10=makeQuery(id+"F3.opShell","OFFSET_EDGE",EDGE,{"disambiguationData":[OSD([subQ0]),TDD([makeQuery(id+"F1.opExtrude","CAP_EDGE",EDGE,{"disambiguationData":[OSD([subQ0])],"isStart":false})])]});}
            var Q11;
            {var subQ0=sQuery(id+"F0.wireOp",EDGE,"E93");Q11=makeQuery(id+"F3.opShell","OFFSET_EDGE",EDGE,{"disambiguationData":[OSD([subQ0]),TDD([makeQuery(id+"F1.opExtrude","CAP_EDGE",EDGE,{"disambiguationData":[OSD([subQ0])],"isStart":false})])]});}
            var Q12;
            {var subQ0=sQuery(id+"F0.wireOp",EDGE,"E94.filletArc");Q12=makeQuery(id+"F3.opShell","OFFSET_EDGE",EDGE,{"disambiguationData":[OSD([subQ0]),TDD([makeQuery(id+"F1.opExtrude","CAP_EDGE",EDGE,{"disambiguationData":[OSD([subQ0])],"isStart":false})])]});}
            var Q13;
            {var subQ0=sQuery(id+"F0.wireOp",EDGE,"E92.left");Q13=makeQuery(id+"F3.opShell","OFFSET_EDGE",EDGE,{"disambiguationData":[OSD([subQ0]),TDD([makeQuery(id+"F1.opExtrude","CAP_EDGE",EDGE,{"disambiguationData":[OSD([subQ0])],"isStart":false})])]});}
            var Q14;
            {var subQ0=sQuery(id+"F0.wireOp",EDGE,"E95.filletArc");Q14=makeQuery(id+"F3.opShell","OFFSET_EDGE",EDGE,{"disambiguationData":[OSD([subQ0]),TDD([makeQuery(id+"F1.opExtrude","CAP_EDGE",EDGE,{"disambiguationData":[OSD([subQ0])],"isStart":false})])]});}
            var Q15;
            {var subQ0=sQuery(id+"F0.wireOp",EDGE,"E92.bottom");Q15=makeQuery(id+"F3.opShell","OFFSET_EDGE",EDGE,{"disambiguationData":[OSD([subQ0]),TDD([makeQuery(id+"F1.opExtrude","CAP_EDGE",EDGE,{"disambiguationData":[OSD([subQ0])],"isStart":false})])]});}
            var Q16;
            {var subQ0=sQuery(id+"F0.wireOp",EDGE,"E91");Q16=makeQuery(id+"F3.opShell","OFFSET_EDGE",EDGE,{"disambiguationData":[OSD([subQ0]),TDD([makeQuery(id+"F1.opExtrude","CAP_EDGE",EDGE,{"disambiguationData":[OSD([subQ0])],"isStart":false})])]});}
            fillet(context, id + "F4", {"entities" : qUnion([Q0, Q1, Q2, Q3, Q4, Q5, Q6, Q7, Q8, Q9, Q10, Q11, Q12, Q13, Q14, Q15, Q16]), "radius" : 1 * mm, "tangentPropagation" : true, "allowEdgeOverflow" : false});
        }
    });
